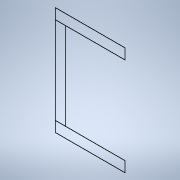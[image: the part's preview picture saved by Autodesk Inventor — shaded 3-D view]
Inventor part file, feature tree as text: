
AUTODESK INVENTOR PART (.ipt)
format: ipt  version: 2022 (Build 260153000, 153)  size: 89,088 bytes
history: native  units: mm
features: sketch x1
ambient origin geometry x8: Origin, YZ Plane, XZ Plane, XY Plane, X Axis, Y Axis, Z Axis, Center Point
feature tree (1):
  sketch  "Sketch4"
